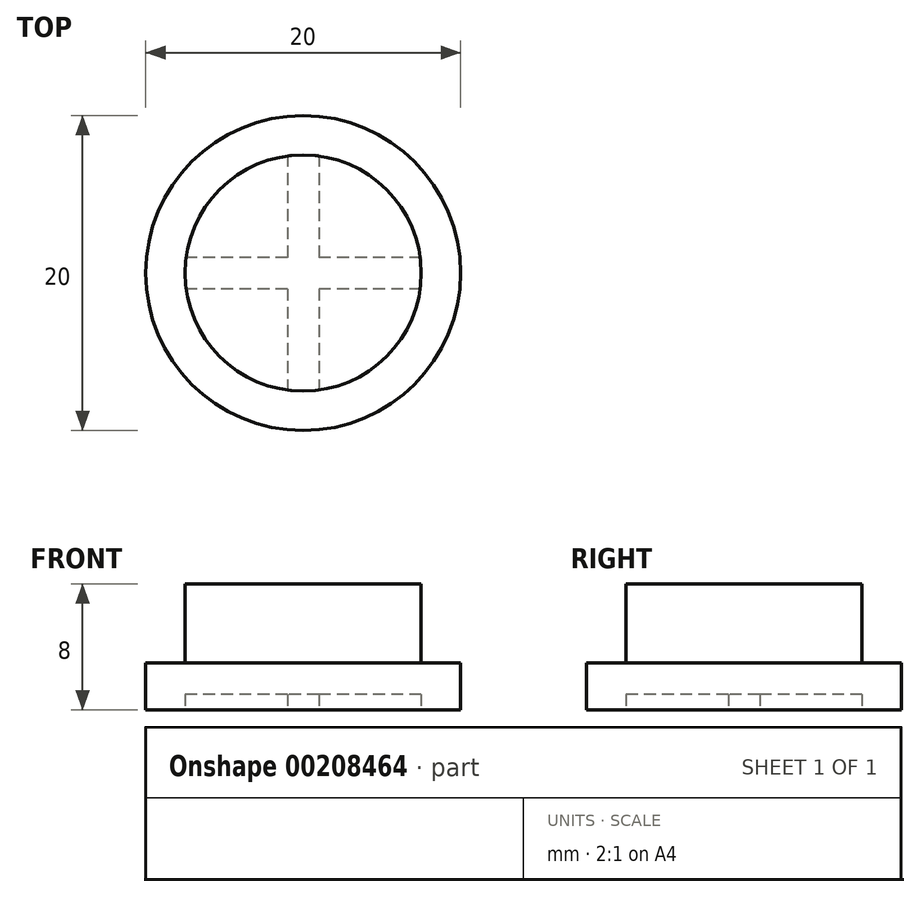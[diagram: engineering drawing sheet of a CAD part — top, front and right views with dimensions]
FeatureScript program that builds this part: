
annotation { "Feature Type Name" : "Feature", "Feature Type Description" : "" }
export const myFeature = defineFeature(function(context is Context, id is Id, definition is map)
    precondition{}
    {
        {
            var Q0;
            Q0=qCreatedBy(makeId("Top.planeOp"),FACE);
            var sketch = newSketch(context, id + "F0", { "sketchPlane" : qUnion([Q0])});
            skCircle(sketch, "E0", {"center": v(0, 0) * mm, "radius": 10 * mm});
            skSolve(sketch);
        }
        {
            var Q0;
            Q0=qSketchRegion(id+"F0",true);
            extrude(context, id + "F1", {"entities" : qUnion([Q0]), "depth" : 3 * mm});
        }
        {
            var Q0;
            Q0=makeQuery(id+"F1.opExtrude","CAP_FACE",FACE,{"disambiguationData":[OSD([sQuery(id+"F0.wireOp",EDGE,"E0")])],"isStart":false});
            var sketch = newSketch(context, id + "F2", { "sketchPlane" : qUnion([Q0])});
            skCircle(sketch, "E1", {"center": v(0, 0) * mm, "radius": 7.5 * mm});
            skSolve(sketch);
        }
        {
            var Q0;
            Q0=qSketchRegion(id+"F2",true);
            extrude(context, id + "F3", {"entities" : qUnion([Q0]), "operationType" : NewBodyOperationType.ADD, "depth" : 5 * mm});
        }
        {
            var Q0;
            Q0=makeQuery(id+"F1.opExtrude","CAP_FACE",FACE,{"disambiguationData":[OSD([sQuery(id+"F0.wireOp",EDGE,"E0")])],"isStart":true});
            var sketch = newSketch(context, id + "F4", { "sketchPlane" : qUnion([Q0])});
            skLineSegment(sketch, "E2.bottom", {"start": v(7.5, -1) * mm, "end": v(-7.5, -1) * mm});
            skLineSegment(sketch, "E2.top", {"start": v(7.5, 1) * mm, "end": v(-7.5, 1) * mm});
            skLineSegment(sketch, "E2.left", {"start": v(7.5, -1) * mm, "end": v(7.5, 1) * mm});
            skLineSegment(sketch, "E2.right", {"start": v(-7.5, -1) * mm, "end": v(-7.5, 1) * mm});
            skPoint(sketch, "E2.middle", {"position": v(0, 0) * mm});
            skLineSegment(sketch, "E3.bottom", {"start": v(1, -7.5) * mm, "end": v(-1, -7.5) * mm});
            skLineSegment(sketch, "E3.top", {"start": v(1, 7.5) * mm, "end": v(-1, 7.5) * mm});
            skLineSegment(sketch, "E3.left", {"start": v(1, -7.5) * mm, "end": v(1, 7.5) * mm});
            skLineSegment(sketch, "E3.right", {"start": v(-1, -7.5) * mm, "end": v(-1, 7.5) * mm});
            skSolve(sketch);
        }
        {
            var Q0;
            Q0=qSketchRegion(id+"F4",true);
            extrude(context, id + "F5", {"entities" : qUnion([Q0]), "operationType" : NewBodyOperationType.REMOVE, "oppositeDirection" : true, "depth" : 1 * mm});
        }
    });
